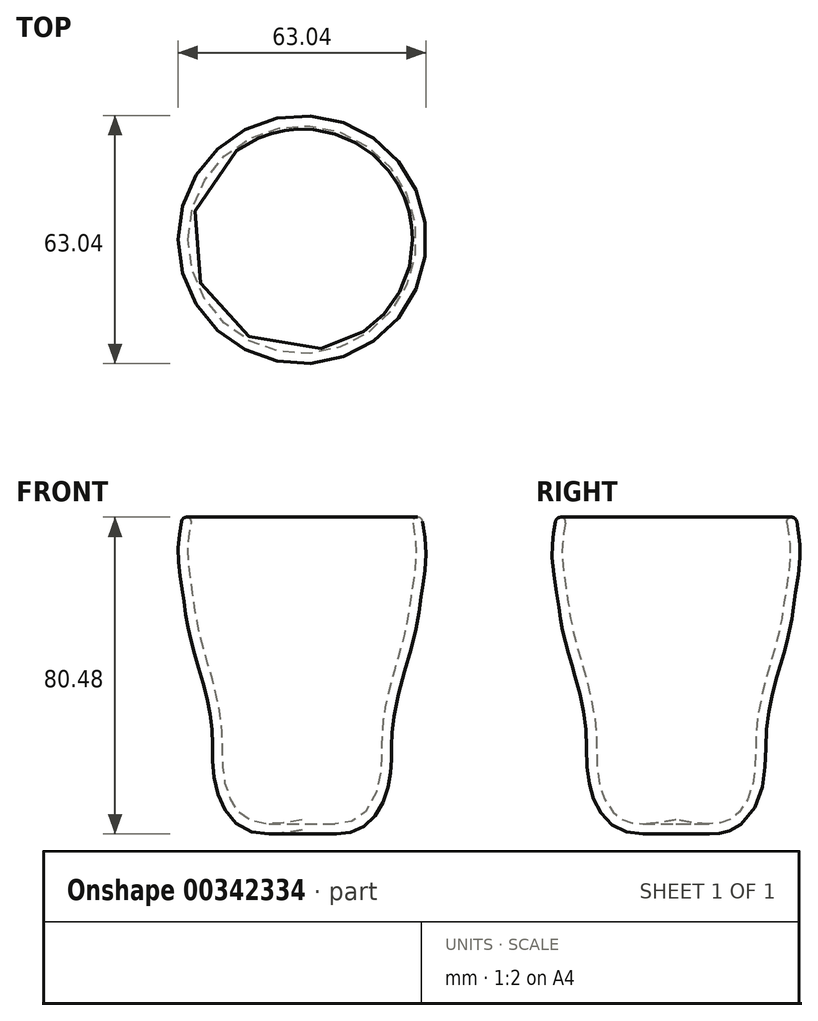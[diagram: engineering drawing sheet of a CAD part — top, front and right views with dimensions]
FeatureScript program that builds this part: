
annotation { "Feature Type Name" : "Feature", "Feature Type Description" : "" }
export const myFeature = defineFeature(function(context is Context, id is Id, definition is map)
    precondition{}
    {
        {
            var Q0;
            Q0=qCreatedBy(makeId("Front.planeOp"),FACE);
            var sketch = newSketch(context, id + "F0", { "sketchPlane" : qUnion([Q0])});
            skFitSpline(sketch, "E0", {"points": [v(0, 0) * mm, v(-13.59, 0) * mm, v(-19.57, 9.62) * mm, v(-20.43, 23.59) * mm, v(-23.56, 38.4) * mm, v(-26.41, 48.95) * mm, v(-27.84, 58.07) * mm, v(-28.98, 67.76) * mm, v(-27.84, 76.89) * mm], "startDerivative": vector(-111.39, -20.05) * mm, "endDerivative": vector(15.52, 80.9) * mm});
            skLineSegment(sketch, "E1", {"start": v(-27.84, 76.89) * mm, "end": v(0, 76.89) * mm});
            skLineSegment(sketch, "E2", {"start": v(0, 76.89) * mm, "end": v(0, 0) * mm});
            skSolve(sketch);
        }
        {
            var Q0;
            Q0=makeQuery(id+"F0.imprint","IMPRINT",FACE,{"disambiguationData":[TD([[makeQuery(id+"F0.imprint","IMPRINT",EDGE,{"derivedFrom":sQuery(id+"F0.wireOp",EDGE,"E0")}),-1.0]])]});
            var Q1;
            Q1=sQuery(id+"F0.wireOp",EDGE,"E2");
            revolve(context, id + "F1", {"entities" : qUnion([Q0]), "axis" : qUnion([Q1]), "revolveType" : RevolveType.FULL});
        }
        {
            var Q0;
            Q0=makeQuery(id+"F1.opRevolve","SWEPT_FACE",FACE,{"disambiguationData":[OSD([sQuery(id+"F0.wireOp",EDGE,"E1")])]});
            shell(context, id + "F2", {"entities" : qUnion([Q0]), "thickness" : 2.54 * mm, "oppositeDirection" : true});
        }
        {
            var Q0;
            Q0=makeQuery(id+"F2.opShell","OFFSET_EDGE",EDGE,{"disambiguationData":[OSD([sQuery(id+"F0.wireOp",EDGE,"E0"),sQuery(id+"F0.wireOp",EDGE,"E1")])]});
            var Q1;
            Q1=makeQuery(id+"F1.opRevolve","SWEPT_EDGE",EDGE,{"disambiguationData":[OSD([sQuery(id+"F0.wireOp",EDGE,"E0"),sQuery(id+"F0.wireOp",EDGE,"E1")])]});
            fillet(context, id + "F3", {"entities" : qUnion([Q0, Q1]), "radius" : 1.27 * mm, "tangentPropagation" : true, "allowEdgeOverflow" : false});
        }
    });
